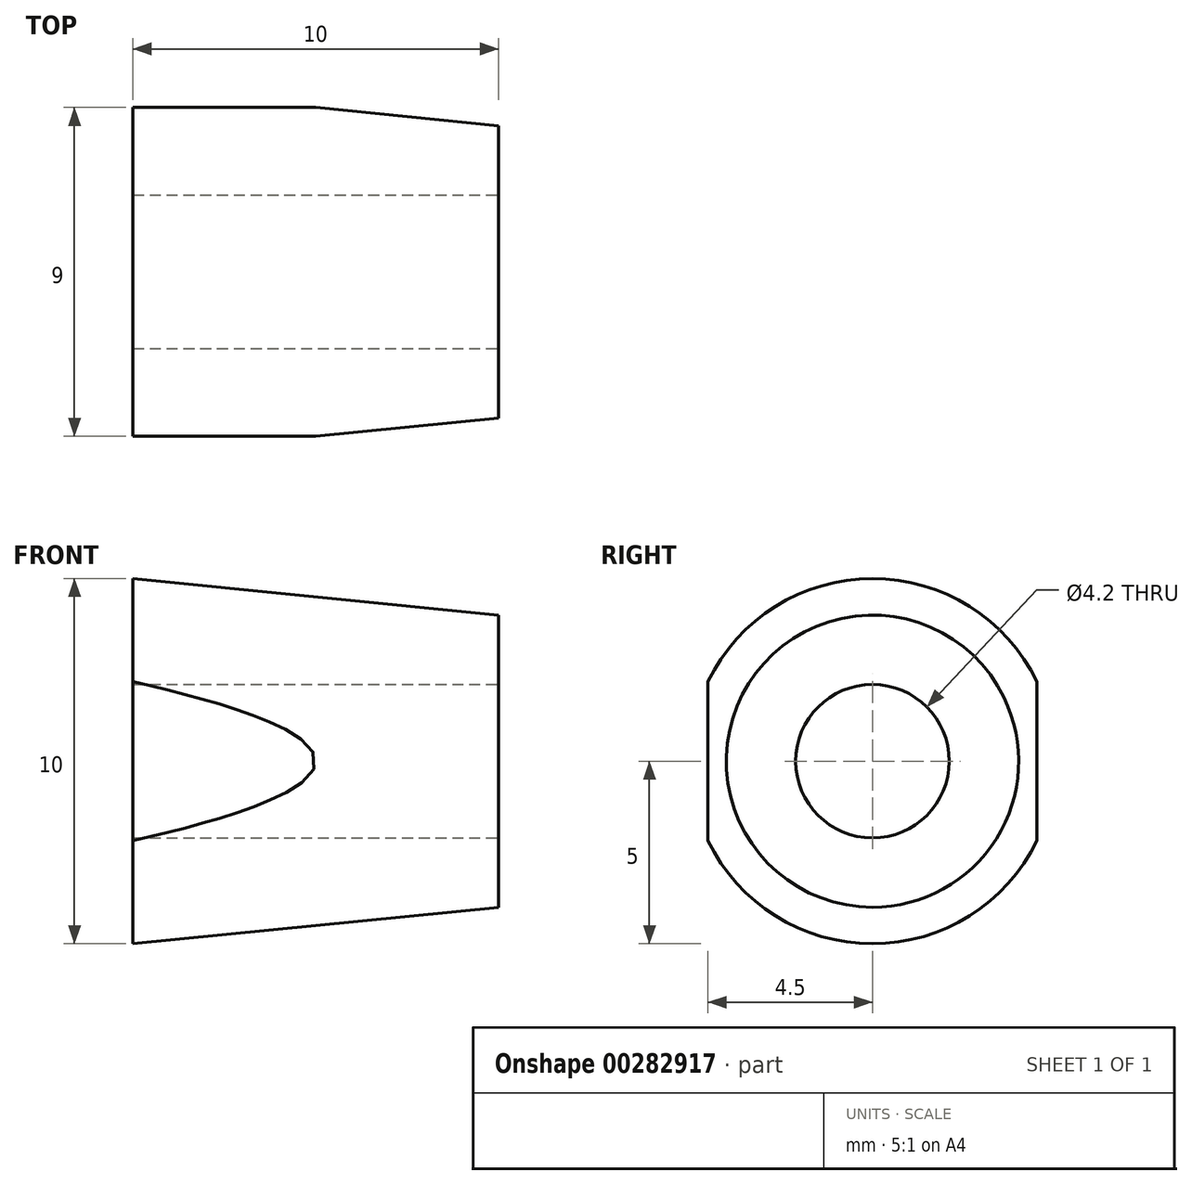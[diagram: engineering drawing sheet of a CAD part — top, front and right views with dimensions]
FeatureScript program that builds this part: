
annotation { "Feature Type Name" : "Feature", "Feature Type Description" : "" }
export const myFeature = defineFeature(function(context is Context, id is Id, definition is map)
    precondition{}
    {
        {
            var Q0;
            Q0=qCreatedBy(makeId("Front.planeOp"),FACE);
            var sketch = newSketch(context, id + "F0", { "sketchPlane" : qUnion([Q0])});
            skLineSegment(sketch, "E0", {"start": v(0, 0) * mm, "end": v(-10, 0) * mm});
            skLineSegment(sketch, "E1", {"start": v(-10, 0) * mm, "end": v(-10, 5) * mm});
            skLineSegment(sketch, "E2", {"start": v(-10, 5) * mm, "end": v(0, 4) * mm});
            skLineSegment(sketch, "E3", {"start": v(0, 4) * mm, "end": v(0, 0) * mm});
            skSolve(sketch);
        }
        {
            var Q0;
            Q0=makeQuery(id+"F0.imprint","IMPRINT",FACE,{"disambiguationData":[TD([[makeQuery(id+"F0.imprint","IMPRINT",EDGE,{"derivedFrom":sQuery(id+"F0.wireOp",EDGE,"E0")}),-1.0]])]});
            var Q1;
            Q1=sQuery(id+"F0.wireOp",EDGE,"E0");
            revolve(context, id + "F1", {"entities" : qUnion([Q0]), "axis" : qUnion([Q1]), "revolveType" : RevolveType.FULL});
        }
        {
            var Q0;
            Q0=makeQuery(id+"F1.opRevolve","SWEPT_FACE",FACE,{"disambiguationData":[OSD([sQuery(id+"F0.wireOp",EDGE,"E3")])]});
            var sketch = newSketch(context, id + "F2", { "sketchPlane" : qUnion([Q0])});
            skLineSegment(sketch, "E4", {"start": v(-4.5, 7.5) * mm, "end": v(-4.5, -7.5) * mm});
            skLineSegment(sketch, "E5", {"start": v(-4.5, -7.5) * mm, "end": v(4.5, -7.5) * mm});
            skLineSegment(sketch, "E6", {"start": v(4.5, -7.5) * mm, "end": v(4.5, 7.5) * mm});
            skLineSegment(sketch, "E7", {"start": v(4.5, 7.5) * mm, "end": v(-4.5, 7.5) * mm});
            skLineSegment(sketch, "E8", {"start": v(0, 0) * mm, "end": v(12, 0) * mm, "construction": true});
            skLineSegment(sketch, "E9", {"start": v(0, 0) * mm, "end": v(0, 13.4) * mm, "construction": true});
            skSolve(sketch);
        }
        {
            var Q0;
            Q0 = qSketchRegion(id + "F2", true);
            extrude(context, id + "F3", {"entities" : qUnion([Q0]), "operationType" : NewBodyOperationType.INTERSECT, "endBound" : BoundingType.THROUGH_ALL, "oppositeDirection" : true, "depth" : 25 * mm});
        }
        {
            var Q0;
            Q0=makeQuery(id+"F1.opRevolve","SWEPT_FACE",FACE,{"disambiguationData":[OSD([sQuery(id+"F0.wireOp",EDGE,"E3")])]});
            var sketch = newSketch(context, id + "F4", { "sketchPlane" : qUnion([Q0])});
            skPoint(sketch, "E10", {"position": v(0, 0) * mm});
            skSolve(sketch);
        }
        {
            var Q0;
            Q0=sQuery(id+"F4.wireOp",VERTEX,"E10");
            var Q1;
            Q1=makeQuery(id+"F1.opRevolve","SWEPT_BODY",BODY,{"disambiguationData":[OSD([sQuery(id+"F0.wireOp",EDGE,"E0"),sQuery(id+"F0.wireOp",EDGE,"E1"),sQuery(id+"F0.wireOp",EDGE,"E2"),sQuery(id+"F0.wireOp",EDGE,"E3")])]});
            hole(context, id + "F5", {"style" : HoleStyle.SIMPLE, "endStyle" : HoleEndStyle.THROUGH, "standardTappedOrClearance" : lookupTablePath({ "standard" : "ISO", "engagement" : "75%", "pitch" : "0.8 mm", "size" : "M5", "type" : "Tapped" }), "standardBlindInLast" : lookupTablePath({ "standard" : "ISO", "engagement" : "75%", "pitch" : "0.8 mm", "size" : "M5", "type" : "Tapped" }), "holeDiameter" : 4.2 * mm, "showTappedDepth" : true, "tappedDepth" : 12 * mm, "tapClearance" : 3, "locations" : qUnion([Q0]), "scope" : qUnion([Q1]), "majorDiameter" : 5 * mm});
        }
    });
